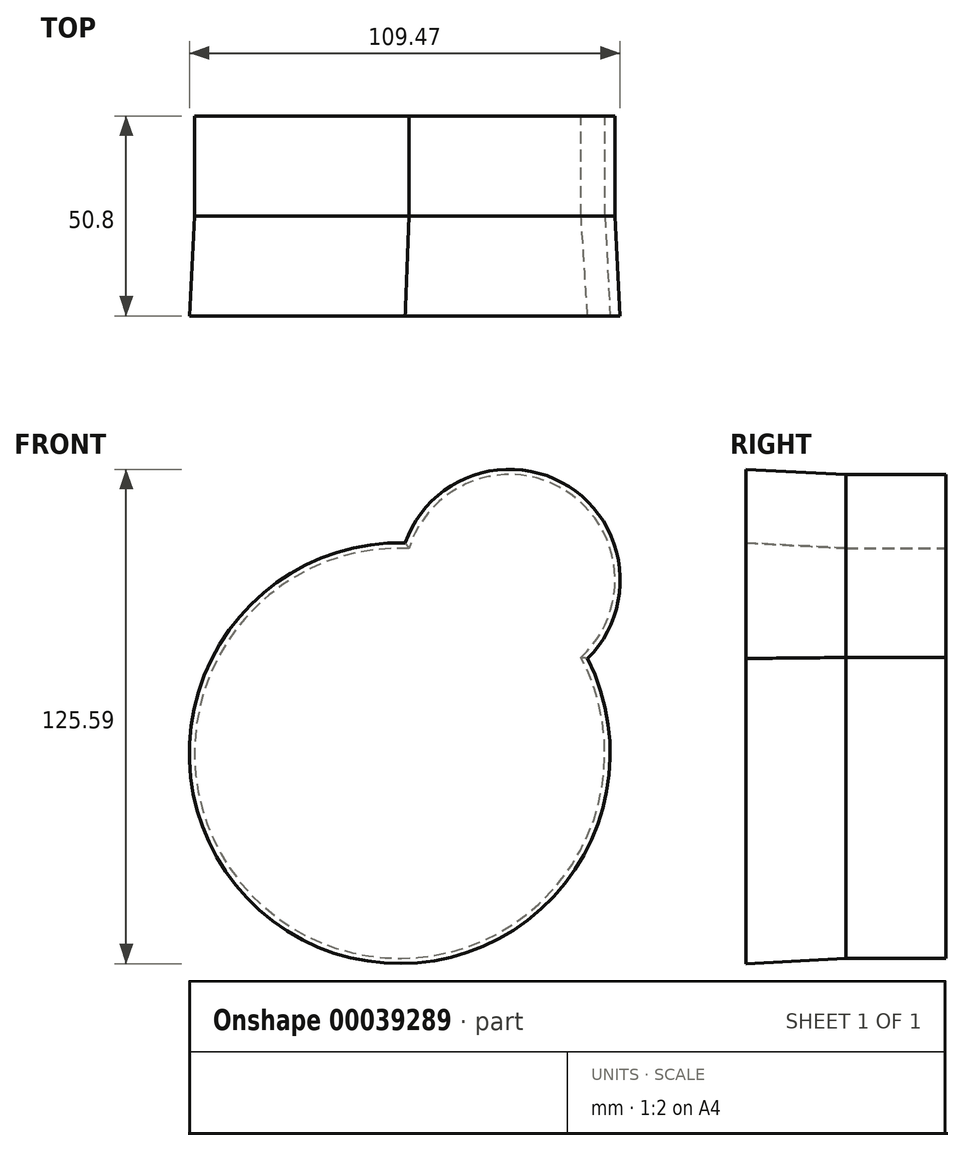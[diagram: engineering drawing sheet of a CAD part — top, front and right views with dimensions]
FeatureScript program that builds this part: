
annotation { "Feature Type Name" : "Feature", "Feature Type Description" : "" }
export const myFeature = defineFeature(function(context is Context, id is Id, definition is map)
    precondition{}
    {
        {
            var Q0;
            Q0=qCreatedBy(makeId("Front.planeOp"),FACE);
            var sketch = newSketch(context, id + "F0", { "sketchPlane" : qUnion([Q0])});
            skCircle(sketch, "E0", {"center": v(0, 0) * mm, "radius": 52.12 * mm});
            skCircle(sketch, "E1", {"center": v(27.9, 44.02) * mm, "radius": 26.79 * mm});
            skSolve(sketch);
        }
        {
            var Q0;
            {var subQ0=sQuery(id+"F0.wireOp",EDGE,"E1");var subQ1=sQuery(id+"F0.wireOp",EDGE,"E0");var subQ3=makeQuery(id+"F0.imprint","INTERSECT",VERTEX,{"disambiguationData":[OD(0.0)],"derivedFrom":[subQ1,subQ0]});Q0=makeQuery(id+"F0.imprint","IMPRINT",FACE,{"disambiguationData":[TD([[makeQuery(id+"F0.imprint","IMPRINT",EDGE,{"disambiguationData":[TD([[subQ3,-1.0]])],"derivedFrom":subQ1}),1.0]])]});}
            var Q1;
            {var subQ0=sQuery(id+"F0.wireOp",EDGE,"E1");var subQ1=sQuery(id+"F0.wireOp",EDGE,"E0");var subQ3=makeQuery(id+"F0.imprint","INTERSECT",VERTEX,{"disambiguationData":[OD(0.0)],"derivedFrom":[subQ1,subQ0]});Q1=makeQuery(id+"F0.imprint","IMPRINT",FACE,{"disambiguationData":[TD([[makeQuery(id+"F0.imprint","IMPRINT",EDGE,{"disambiguationData":[TD([[subQ3,1.0]])],"derivedFrom":subQ1}),-1.0]])]});}
            var Q2;
            {var subQ0=sQuery(id+"F0.wireOp",EDGE,"E1");var subQ1=sQuery(id+"F0.wireOp",EDGE,"E0");var subQ3=makeQuery(id+"F0.imprint","INTERSECT",VERTEX,{"disambiguationData":[OD(0.0)],"derivedFrom":[subQ1,subQ0]});Q2=makeQuery(id+"F0.imprint","IMPRINT",FACE,{"disambiguationData":[TD([[makeQuery(id+"F0.imprint","IMPRINT",EDGE,{"disambiguationData":[TD([[subQ3,1.0]])],"derivedFrom":subQ1}),1.0]])]});}
            extrude(context, id + "F1", {"entities" : qUnion([Q0, Q1, Q2]), "depth" : 25.4 * mm});
        }
        {
            var Q0;
            Q0=makeQuery(id+"F1.opExtrude","CAP_FACE",FACE,{"disambiguationData":[OSD([sQuery(id+"F0.wireOp",EDGE,"E0"),sQuery(id+"F0.wireOp",EDGE,"E1")])],"isStart":false});
            extrude(context, id + "F2", {"entities" : qUnion([Q0]), "operationType" : NewBodyOperationType.ADD, "depth" : 25.4 * mm, "hasDraft" : true, "draftAngle" : 3 * degree});
        }
    });
